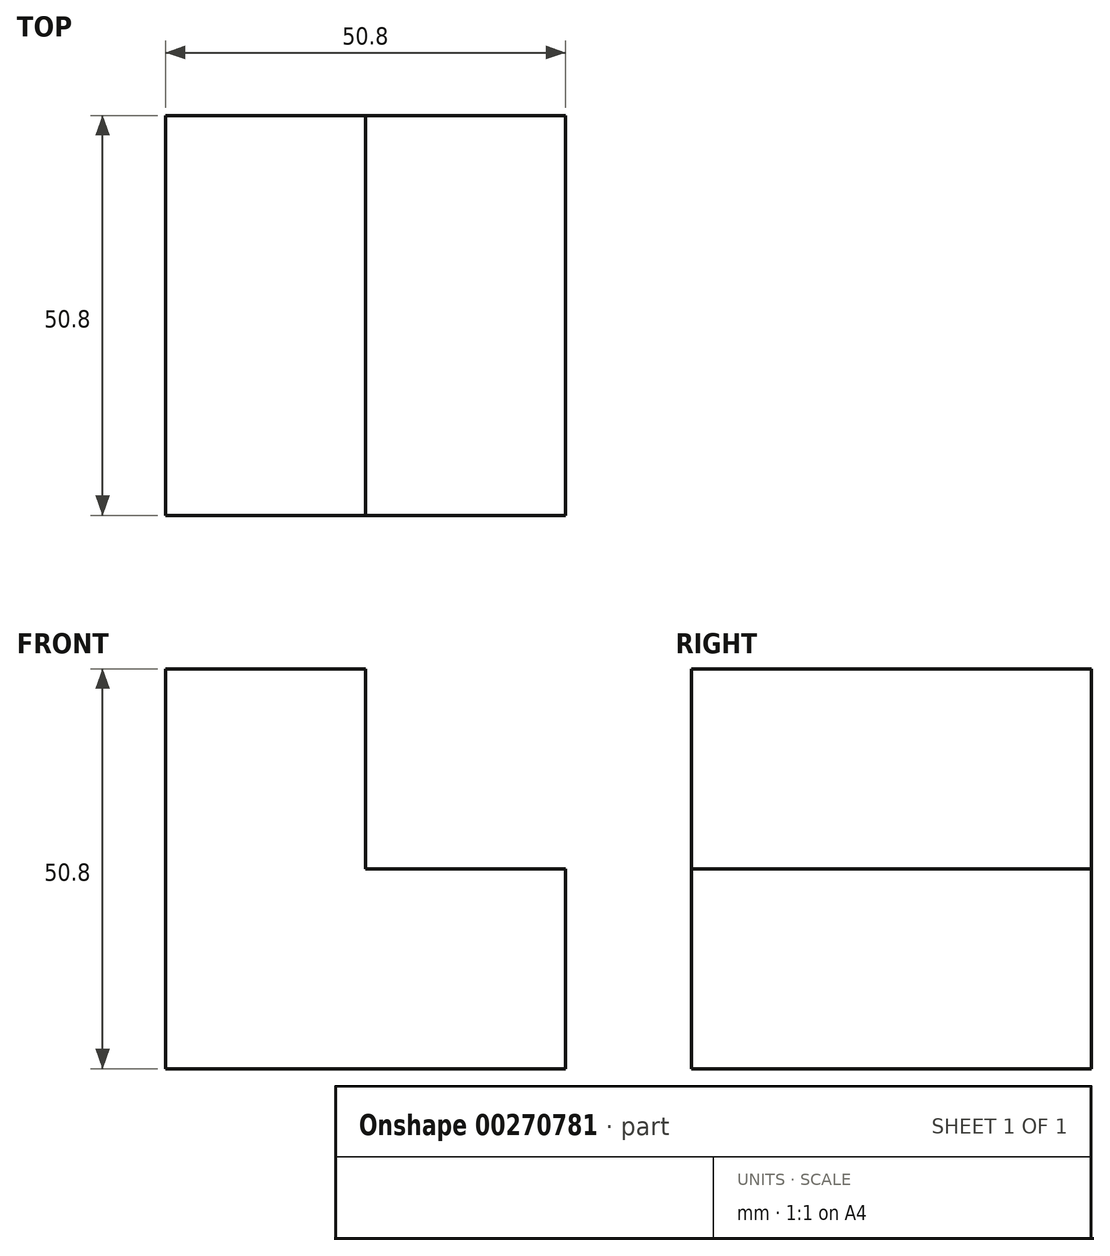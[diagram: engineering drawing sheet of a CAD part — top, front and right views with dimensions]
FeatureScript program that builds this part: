
annotation { "Feature Type Name" : "Feature", "Feature Type Description" : "" }
export const myFeature = defineFeature(function(context is Context, id is Id, definition is map)
    precondition{}
    {
        {
            var Q0;
            Q0=qCreatedBy(makeId("Front.planeOp"),FACE);
            var sketch = newSketch(context, id + "F0", { "sketchPlane" : qUnion([Q0])});
            skLineSegment(sketch, "E0", {"start": v(-56.71, 47.36) * mm, "end": v(-31.31, 47.36) * mm});
            skLineSegment(sketch, "E1", {"start": v(-31.31, 47.36) * mm, "end": v(-31.31, 21.96) * mm});
            skLineSegment(sketch, "E2", {"start": v(-31.31, 21.96) * mm, "end": v(-5.91, 21.96) * mm});
            skLineSegment(sketch, "E3", {"start": v(-5.91, 21.96) * mm, "end": v(-5.91, -3.44) * mm});
            skLineSegment(sketch, "E4", {"start": v(-5.91, -3.44) * mm, "end": v(-56.71, -3.44) * mm});
            skLineSegment(sketch, "E5", {"start": v(-56.71, 47.36) * mm, "end": v(-56.71, -3.44) * mm});
            skSolve(sketch);
        }
        {
            var Q0;
            Q0 = qSketchRegion(id + "F0", true);
            extrude(context, id + "F1", {"entities" : qUnion([Q0]), "depth" : 50.8 * mm});
        }
    });
